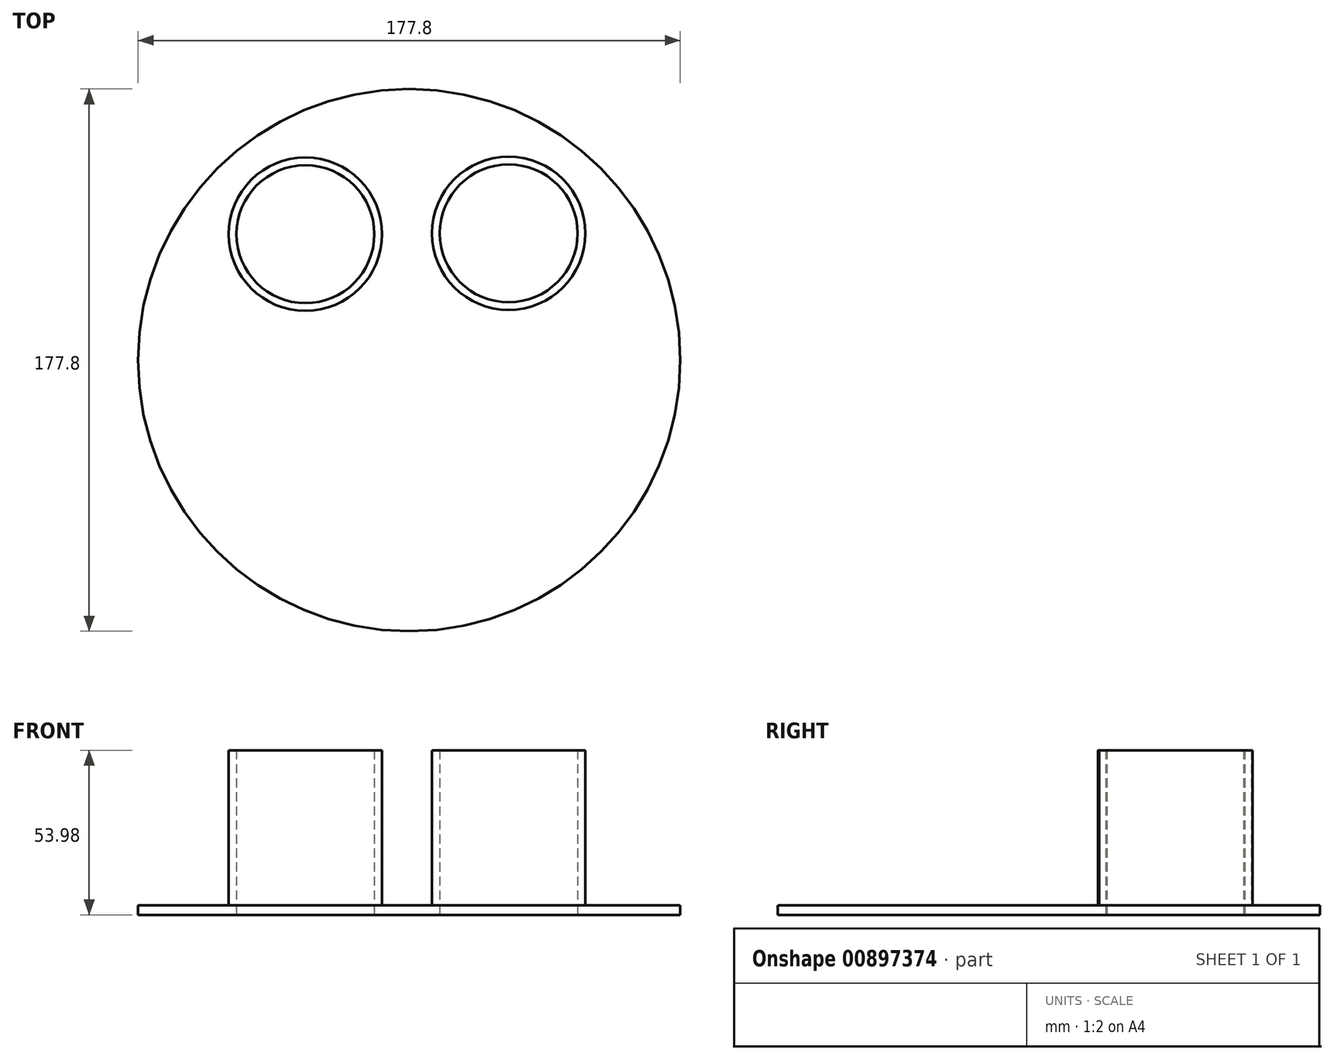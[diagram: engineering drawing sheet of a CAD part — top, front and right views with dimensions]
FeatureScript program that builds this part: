
annotation { "Feature Type Name" : "Feature", "Feature Type Description" : "" }
export const myFeature = defineFeature(function(context is Context, id is Id, definition is map)
    precondition{}
    {
        {
            var Q0;
            Q0=qCreatedBy(makeId("Top.planeOp"),FACE);
            var sketch = newSketch(context, id + "F0", { "sketchPlane" : qUnion([Q0])});
            skCircle(sketch, "E0", {"center": v(0, 0) * mm, "radius": 88.9 * mm});
            skSolve(sketch);
        }
        {
            var Q0;
            Q0=makeQuery(id+"F0.imprint","IMPRINT",FACE,{"disambiguationData":[TD([[makeQuery(id+"F0.imprint","IMPRINT",EDGE,{"derivedFrom":sQuery(id+"F0.wireOp",EDGE,"E0")}),1.0]])]});
            extrude(context, id + "F1", {"entities" : qUnion([Q0]), "depth" : 3.17 * mm, "offsetDistance" : 25.4 * mm});
        }
        {
            var Q0;
            Q0=qCreatedBy(makeId("Top.planeOp"),FACE);
            var sketch = newSketch(context, id + "F2", { "sketchPlane" : qUnion([Q0])});
            skCircle(sketch, "E1", {"center": v(-34.02, 41.3) * mm, "radius": 22.6 * mm});
            skCircle(sketch, "E2", {"center": v(-34.02, 41.3) * mm, "radius": 25.15 * mm});
            skCircle(sketch, "E3", {"center": v(32.64, 41.59) * mm, "radius": 22.6 * mm});
            skCircle(sketch, "E4", {"center": v(32.64, 41.59) * mm, "radius": 25.15 * mm});
            skSolve(sketch);
        }
        {
            var Q0;
            Q0 = qSketchRegion(id + "F2", true);
            extrude(context, id + "F3", {"entities" : qUnion([Q0]), "operationType" : NewBodyOperationType.ADD, "depth" : 53.97 * mm, "offsetDistance" : 25.4 * mm});
        }
        {
            var Q0;
            Q0=makeQuery(id+"F3.boolean.opBoolean","SPLIT",FACE,{"disambiguationData":[TD([makeQuery(id+"F3.opExtrude","SWEPT_FACE",FACE,{"disambiguationData":[OSD([sQuery(id+"F2.wireOp",EDGE,"E1")])]})])],"derivedFrom":makeQuery(id+"F1.opExtrude","CAP_FACE",FACE,{"disambiguationData":[OSD([sQuery(id+"F0.wireOp",EDGE,"E0")])],"isStart":false})});
            extrude(context, id + "F4", {"entities" : qUnion([Q0]), "operationType" : NewBodyOperationType.REMOVE, "endBound" : BoundingType.SYMMETRIC, "oppositeDirection" : true, "depth" : 25.4 * mm, "offsetDistance" : 25.4 * mm});
        }
        {
            var Q0;
            Q0=makeQuery(id+"F3.boolean.opBoolean","SPLIT",FACE,{"disambiguationData":[TD([makeQuery(id+"F3.opExtrude","SWEPT_FACE",FACE,{"disambiguationData":[OSD([sQuery(id+"F2.wireOp",EDGE,"E3")])]})])],"derivedFrom":makeQuery(id+"F1.opExtrude","CAP_FACE",FACE,{"disambiguationData":[OSD([sQuery(id+"F0.wireOp",EDGE,"E0")])],"isStart":false})});
            extrude(context, id + "F5", {"entities" : qUnion([Q0]), "operationType" : NewBodyOperationType.REMOVE, "endBound" : BoundingType.SYMMETRIC, "oppositeDirection" : true, "depth" : 25.4 * mm, "offsetDistance" : 25.4 * mm});
        }
    });
